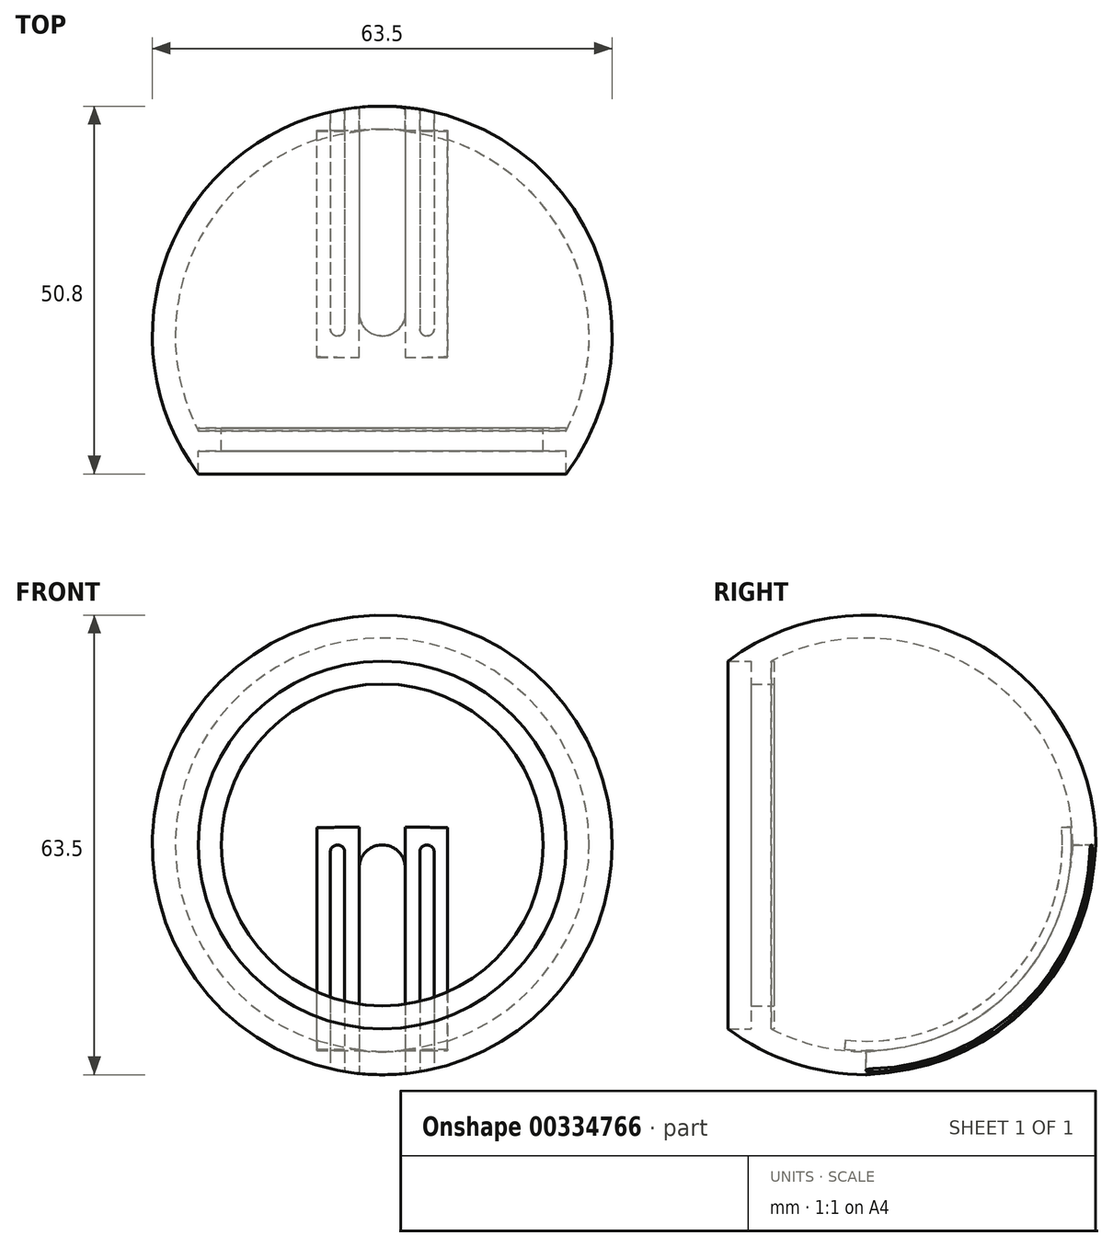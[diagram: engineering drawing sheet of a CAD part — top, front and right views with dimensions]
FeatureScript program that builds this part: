
annotation { "Feature Type Name" : "Feature", "Feature Type Description" : "" }
export const myFeature = defineFeature(function(context is Context, id is Id, definition is map)
    precondition{}
    {
        {
            var Q0;
            Q0=qCreatedBy(makeId("Top.planeOp"),FACE);
            var sketch = newSketch(context, id + "F0", { "sketchPlane" : qUnion([Q0])});
            skArc(sketch, "E0", {"start": v(25.4, -19.05) * mm, "mid": v(0, 31.75) * mm, "end": v(-25.4, -19.05) * mm});
            skLineSegment(sketch, "E1", {"start": v(0, 31.75) * mm, "end": v(0, -31.75) * mm});
            skArc(sketch, "E2.0", {"start": v(23.76, -15.87) * mm, "mid": v(0, 28.57) * mm, "end": v(-23.76, -15.87) * mm});
            skLineSegment(sketch, "E3", {"start": v(25.4, -15.87) * mm, "end": v(25.4, -19.05) * mm});
            skLineSegment(sketch, "E4", {"start": v(-25.4, -15.87) * mm, "end": v(-25.4, -19.05) * mm});
            skLineSegment(sketch, "E5", {"start": v(25.4, -15.87) * mm, "end": v(25.4, -12.7) * mm});
            skLineSegment(sketch, "E6", {"start": v(25.4, -12.7) * mm, "end": v(22.23, -12.7) * mm});
            skLineSegment(sketch, "E7", {"start": v(22.23, -12.7) * mm, "end": v(22.23, -15.87) * mm});
            skLineSegment(sketch, "E8", {"start": v(25.4, -15.87) * mm, "end": v(22.23, -15.87) * mm});
            skLineSegment(sketch, "E9.MirrorCS", {"start": v(-25.4, -12.7) * mm, "end": v(-22.23, -12.7) * mm});
            skLineSegment(sketch, "E10.MirrorCS", {"start": v(-22.23, -12.7) * mm, "end": v(-22.23, -15.87) * mm});
            skLineSegment(sketch, "E11.MirrorCS", {"start": v(-25.4, -15.87) * mm, "end": v(-22.23, -15.87) * mm});
            skLineSegment(sketch, "E12.MirrorCS", {"start": v(-25.4, -15.87) * mm, "end": v(-25.4, -12.7) * mm});
            skSolve(sketch);
        }
        {
            var Q0;
            {var subQ1=sQuery(id+"F0.wireOp",EDGE,"E6");Q0=makeQuery(id+"F0.imprint","IMPRINT",FACE,{"disambiguationData":[TD([[makeQuery(id+"F0.imprint","IMPRINT",EDGE,{"derivedFrom":subQ1}),1.0]])]});}
            var Q1;
            {var subQ0=sQuery(id+"F0.wireOp",EDGE,"E8");var subQ1=sQuery(id+"F0.wireOp",EDGE,"E2.0");var subQ2=makeQuery(id+"F0.imprint","INTERSECT",VERTEX,{"derivedFrom":[subQ1,subQ0]});Q1=makeQuery(id+"F0.imprint","IMPRINT",FACE,{"disambiguationData":[TD([[makeQuery(id+"F0.imprint","IMPRINT",EDGE,{"disambiguationData":[TD([[subQ2,-1.0]])],"derivedFrom":subQ1}),-1.0]])]});}
            var Q2;
            {var subQ5=sQuery(id+"F0.wireOp",EDGE,"E3");Q2=makeQuery(id+"F0.imprint","IMPRINT",FACE,{"disambiguationData":[TD([[makeQuery(id+"F0.imprint","IMPRINT",EDGE,{"derivedFrom":subQ5}),1.0]])]});}
            var Q3;
            Q3=sQuery(id+"F0.wireOp",EDGE,"E1");
            revolve(context, id + "F1", {"entities" : qUnion([Q0, Q1, Q2]), "axis" : qUnion([Q3]), "revolveType" : RevolveType.FULL});
        }
        {
            var Q0;
            Q0=qCreatedBy(makeId("Front.planeOp"),FACE);
            var Q1;
            Q1=qCreatedBy(makeId("Top.planeOp"),FACE);
            cPlane(context, id + "F2", {"entities" : qUnion([Q0, Q1]), "cplaneType" : CPlaneType.MID_PLANE, "offset" : 25.4 * mm, "width" : 152.4 * mm, "height" : 152.4 * mm});
        }
        {
            var Q0;
            Q0=qCreatedBy(id+"F2.planeOp",FACE);
            var sketch = newSketch(context, id + "F3", { "sketchPlane" : qUnion([Q0])});
            skLineSegment(sketch, "E13.bottom", {"start": v(-3.18, -27.79) * mm, "end": v(3.17, -27.79) * mm});
            skLineSegment(sketch, "E13.top", {"start": v(-3.18, -34.51) * mm, "end": v(3.17, -34.51) * mm});
            skLineSegment(sketch, "E13.left", {"start": v(-3.18, -27.79) * mm, "end": v(-3.18, -34.51) * mm});
            skLineSegment(sketch, "E13.right", {"start": v(3.17, -27.79) * mm, "end": v(3.17, -34.51) * mm});
            skLineSegment(sketch, "E14", {"start": v(-18.25, 0) * mm, "end": v(17.68, 0) * mm});
            skLineSegment(sketch, "E15.bottom", {"start": v(5.18, -27.8) * mm, "end": v(7.18, -27.8) * mm});
            skLineSegment(sketch, "E15.top", {"start": v(5.18, -34.8) * mm, "end": v(7.18, -34.8) * mm});
            skLineSegment(sketch, "E15.left", {"start": v(5.18, -27.8) * mm, "end": v(5.18, -34.8) * mm});
            skLineSegment(sketch, "E15.right", {"start": v(7.18, -27.8) * mm, "end": v(7.18, -34.8) * mm});
            skLineSegment(sketch, "E16.MirrorCS", {"start": v(-7.18, -27.8) * mm, "end": v(-7.18, -34.8) * mm});
            skLineSegment(sketch, "E17.MirrorCS", {"start": v(-5.18, -34.8) * mm, "end": v(-7.18, -34.8) * mm});
            skLineSegment(sketch, "E18.MirrorCS", {"start": v(-5.18, -27.8) * mm, "end": v(-7.18, -27.8) * mm});
            skLineSegment(sketch, "E19.MirrorCS", {"start": v(-5.18, -27.8) * mm, "end": v(-5.18, -34.8) * mm});
            skLineSegment(sketch, "E20", {"start": v(0, -45.26) * mm, "end": v(0, -2) * mm});
            skPoint(sketch, "E20.endSnap0", {"position": v(0, -27.79) * mm});
            skSolve(sketch);
        }
        {
            var Q0;
            Q0=makeQuery(id+"F3.imprint","IMPRINT",FACE,{"disambiguationData":[TD([[makeQuery(id+"F3.imprint","IMPRINT",EDGE,{"derivedFrom":sQuery(id+"F3.wireOp",EDGE,"E13.bottom")}),-1.0]])]});
            var Q1;
            Q1=makeQuery(id+"F3.imprint","IMPRINT",FACE,{"disambiguationData":[TD([[makeQuery(id+"F3.imprint","IMPRINT",EDGE,{"derivedFrom":sQuery(id+"F3.wireOp",EDGE,"E16.MirrorCS")}),1.0]])]});
            var Q2;
            Q2=makeQuery(id+"F3.imprint","IMPRINT",FACE,{"disambiguationData":[TD([[makeQuery(id+"F3.imprint","IMPRINT",EDGE,{"derivedFrom":sQuery(id+"F3.wireOp",EDGE,"E15.bottom")}),-1.0]])]});
            var Q3;
            Q3=sQuery(id+"F3.wireOp",EDGE,"E14");
            revolve(context, id + "F4", {"operationType" : NewBodyOperationType.REMOVE, "entities" : qUnion([Q0, Q1, Q2]), "axis" : qUnion([Q3]), "revolveType" : RevolveType.TWO_DIRECTIONS, "angle" : 45 * degree, "angleBack" : 315 * degree});
        }
        {
            var Q0;
            Q0=makeQuery(id+"F4.boolean.opBoolean","COPY",EDGE,{"derivedFrom":makeQuery(id+"F4.opRevolve","CAP_EDGE",EDGE,{"disambiguationData":[OSD([sQuery(id+"F3.wireOp",EDGE,"E13.right")])],"isStart":true})});
            var Q1;
            Q1=makeQuery(id+"F4.boolean.opBoolean","COPY",EDGE,{"derivedFrom":makeQuery(id+"F4.opRevolve","CAP_EDGE",EDGE,{"disambiguationData":[OSD([sQuery(id+"F3.wireOp",EDGE,"E13.left")])],"isStart":true})});
            var Q2;
            Q2=makeQuery(id+"F4.boolean.opBoolean","COPY",EDGE,{"derivedFrom":makeQuery(id+"F4.opRevolve","CAP_EDGE",EDGE,{"disambiguationData":[OSD([sQuery(id+"F3.wireOp",EDGE,"E13.right")])],"isStart":false})});
            var Q3;
            Q3=makeQuery(id+"F4.boolean.opBoolean","COPY",EDGE,{"derivedFrom":makeQuery(id+"F4.opRevolve","CAP_EDGE",EDGE,{"disambiguationData":[OSD([sQuery(id+"F3.wireOp",EDGE,"E13.left")])],"isStart":false})});
            fillet(context, id + "F5", {"entities" : qUnion([Q0, Q1, Q2, Q3]), "radius" : 3.17 * mm, "tangentPropagation" : true, "allowEdgeOverflow" : false});
        }
        {
            var Q0;
            Q0=makeQuery(id+"F4.boolean.opBoolean","COPY",EDGE,{"derivedFrom":makeQuery(id+"F4.opRevolve","CAP_EDGE",EDGE,{"disambiguationData":[OSD([sQuery(id+"F3.wireOp",EDGE,"E19.MirrorCS")])],"isStart":true})});
            var Q1;
            Q1=makeQuery(id+"F4.boolean.opBoolean","COPY",EDGE,{"derivedFrom":makeQuery(id+"F4.opRevolve","CAP_EDGE",EDGE,{"disambiguationData":[OSD([sQuery(id+"F3.wireOp",EDGE,"E16.MirrorCS")])],"isStart":true})});
            var Q2;
            Q2=makeQuery(id+"F4.boolean.opBoolean","COPY",EDGE,{"derivedFrom":makeQuery(id+"F4.opRevolve","CAP_EDGE",EDGE,{"disambiguationData":[OSD([sQuery(id+"F3.wireOp",EDGE,"E15.left")])],"isStart":true})});
            var Q3;
            Q3=makeQuery(id+"F4.boolean.opBoolean","COPY",EDGE,{"derivedFrom":makeQuery(id+"F4.opRevolve","CAP_EDGE",EDGE,{"disambiguationData":[OSD([sQuery(id+"F3.wireOp",EDGE,"E15.right")])],"isStart":true})});
            var Q4;
            Q4=makeQuery(id+"F4.boolean.opBoolean","COPY",EDGE,{"derivedFrom":makeQuery(id+"F4.opRevolve","CAP_EDGE",EDGE,{"disambiguationData":[OSD([sQuery(id+"F3.wireOp",EDGE,"E19.MirrorCS")])],"isStart":false})});
            var Q5;
            Q5=makeQuery(id+"F4.boolean.opBoolean","COPY",EDGE,{"derivedFrom":makeQuery(id+"F4.opRevolve","CAP_EDGE",EDGE,{"disambiguationData":[OSD([sQuery(id+"F3.wireOp",EDGE,"E16.MirrorCS")])],"isStart":false})});
            var Q6;
            Q6=makeQuery(id+"F4.boolean.opBoolean","COPY",EDGE,{"derivedFrom":makeQuery(id+"F4.opRevolve","CAP_EDGE",EDGE,{"disambiguationData":[OSD([sQuery(id+"F3.wireOp",EDGE,"E15.left")])],"isStart":false})});
            var Q7;
            Q7=makeQuery(id+"F4.boolean.opBoolean","COPY",EDGE,{"derivedFrom":makeQuery(id+"F4.opRevolve","CAP_EDGE",EDGE,{"disambiguationData":[OSD([sQuery(id+"F3.wireOp",EDGE,"E15.right")])],"isStart":false})});
            fillet(context, id + "F6", {"entities" : qUnion([Q0, Q1, Q2, Q3, Q4, Q5, Q6, Q7]), "radius" : 2 / 2 * mm, "tangentPropagation" : true, "allowEdgeOverflow" : false});
        }
        {
            var Q0;
            Q0=qCreatedBy(id+"F2.planeOp",FACE);
            var sketch = newSketch(context, id + "F7", { "sketchPlane" : qUnion([Q0])});
            skLineSegment(sketch, "E21", {"start": v(-9, -28.4) * mm, "end": v(9, -28.4) * mm});
            skLineSegment(sketch, "E22", {"start": v(9, -28.4) * mm, "end": v(9, -23.76) * mm});
            skLineSegment(sketch, "E23", {"start": v(9, -23.76) * mm, "end": v(-9, -23.76) * mm});
            skLineSegment(sketch, "E24", {"start": v(-9, -23.76) * mm, "end": v(-9, -28.4) * mm});
            skSolve(sketch);
        }
        {
            var Q0;
            Q0 = qSketchRegion(id + "F7", true);
            var Q1;
            Q1=sQuery(id+"F3.wireOp",EDGE,"E14");
            revolve(context, id + "F8", {"operationType" : NewBodyOperationType.REMOVE, "entities" : qUnion([Q0]), "axis" : qUnion([Q1]), "revolveType" : RevolveType.TWO_DIRECTIONS, "oppositeDirection" : true, "angle" : 51 * degree, "angleBack" : 310 * degree});
        }
    });
